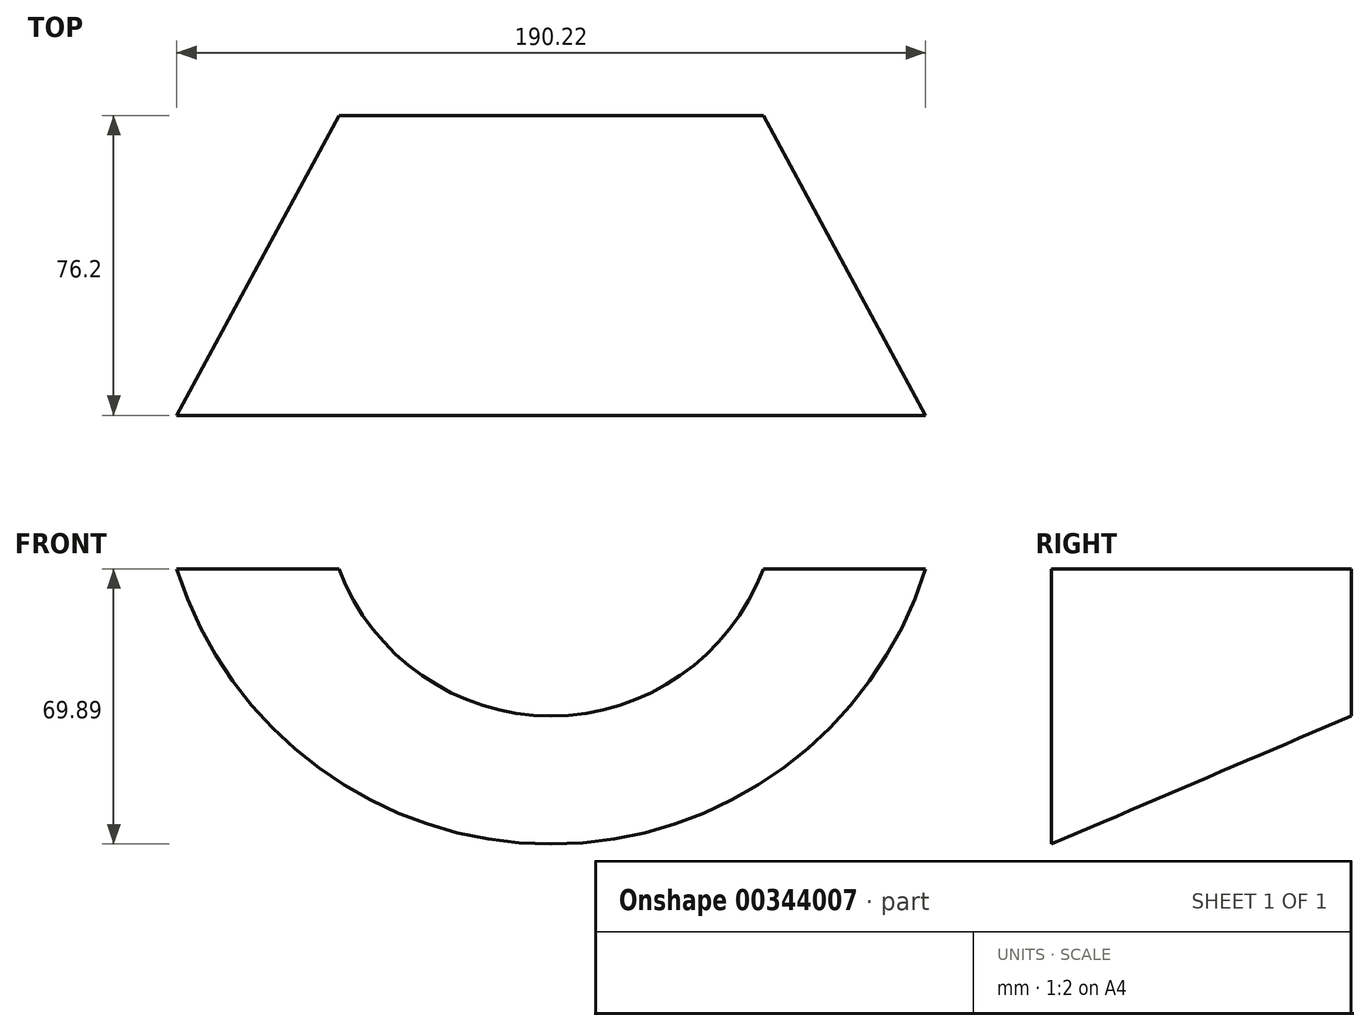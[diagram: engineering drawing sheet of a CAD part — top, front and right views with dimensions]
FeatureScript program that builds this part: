
annotation { "Feature Type Name" : "Feature", "Feature Type Description" : "" }
export const myFeature = defineFeature(function(context is Context, id is Id, definition is map)
    precondition{}
    {
        {
            var Q0;
            Q0=qCreatedBy(makeId("Front.planeOp"),FACE);
            var sketch = newSketch(context, id + "F0", { "sketchPlane" : qUnion([Q0])});
            skLineSegment(sketch, "E0", {"start": v(0, 0) * mm, "end": v(53.92, 0) * mm});
            skLineSegment(sketch, "E1.MirrorCS", {"start": v(0, 0) * mm, "end": v(-53.92, 0) * mm});
            skArc(sketch, "E2", {"start": v(-53.92, 0) * mm, "mid": v(0, -37.33) * mm, "end": v(53.92, 0) * mm});
            skSolve(sketch);
        }
        {
            var Q0;
            Q0=qCreatedBy(makeId("Front.planeOp"),FACE);
            cPlane(context, id + "F1", {"entities" : qUnion([Q0]), "cplaneType" : CPlaneType.OFFSET, "offset" : 76.2 * mm, "width" : 152.4 * mm, "height" : 152.4 * mm});
        }
        {
            var Q0;
            Q0=qCreatedBy(id+"F1.planeOp",FACE);
            var sketch = newSketch(context, id + "F2", { "sketchPlane" : qUnion([Q0])});
            skLineSegment(sketch, "E3", {"start": v(0, 0) * mm, "end": v(-95.11, 0) * mm});
            skLineSegment(sketch, "E4.MirrorCS", {"start": v(0, 0) * mm, "end": v(95.11, 0) * mm});
            skArc(sketch, "E5", {"start": v(-95.11, 0) * mm, "mid": v(0, -69.9) * mm, "end": v(95.11, 0) * mm});
            skSolve(sketch);
        }
        {
            var Q0;
            Q0=sQuery(id+"F2.wireOp",EDGE,"E5");
            var Q1;
            Q1=sQuery(id+"F0.wireOp",EDGE,"E2");
            loft(context, id + "F3", {"bodyType" : ToolBodyType.SURFACE, "wireProfilesArray" : [{ "wireProfileEntities" : qUnion([Q0]) }, { "wireProfileEntities" : qUnion([Q1]) }]});
        }
    });
